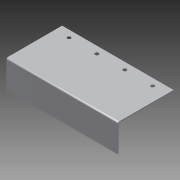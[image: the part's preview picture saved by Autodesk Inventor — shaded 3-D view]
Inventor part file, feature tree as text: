
AUTODESK INVENTOR PART (.ipt)
format: ipt  version: 2013 (Build 170138000, 138)  size: 108,544 bytes
history: native  units: in
note: dims shown in document units (in); Inventor stores cm internally (conversion verified against a paired STEP export)
features: sheet_metal_op x4, sketch x2, other x2
ambient origin geometry x8: Origin, YZ Plane, XZ Plane, XY Plane, X Axis, Y Axis, Z Axis, Center Point
bodies: Solid1 (feature_tree)
feature tree (8):
  sheet_metal_op  "Face1"
  sheet_metal_op  "Flange1"
  sketch  "Sketch1"  dims[d0=2.0in]
  other  "Plate1"
  sketch  "Sketch2"  dims[d1=0.26in d2=0.26in d3=1.0in d4=2.0in d6=2.0in d7=2.0in d8=3.0in d9=8.0in d10=0.0625in d11=0.0625in d12=0.0312in d13=0.125in d14=0.0625in d15=2.0in d16=90.0deg d17=0.05in d18=0.25in d19=0.0625in d20=0.0625in]
  other  "Plate2"
  sheet_metal_op  "Bend1"
  sheet_metal_op  "Corner1"
